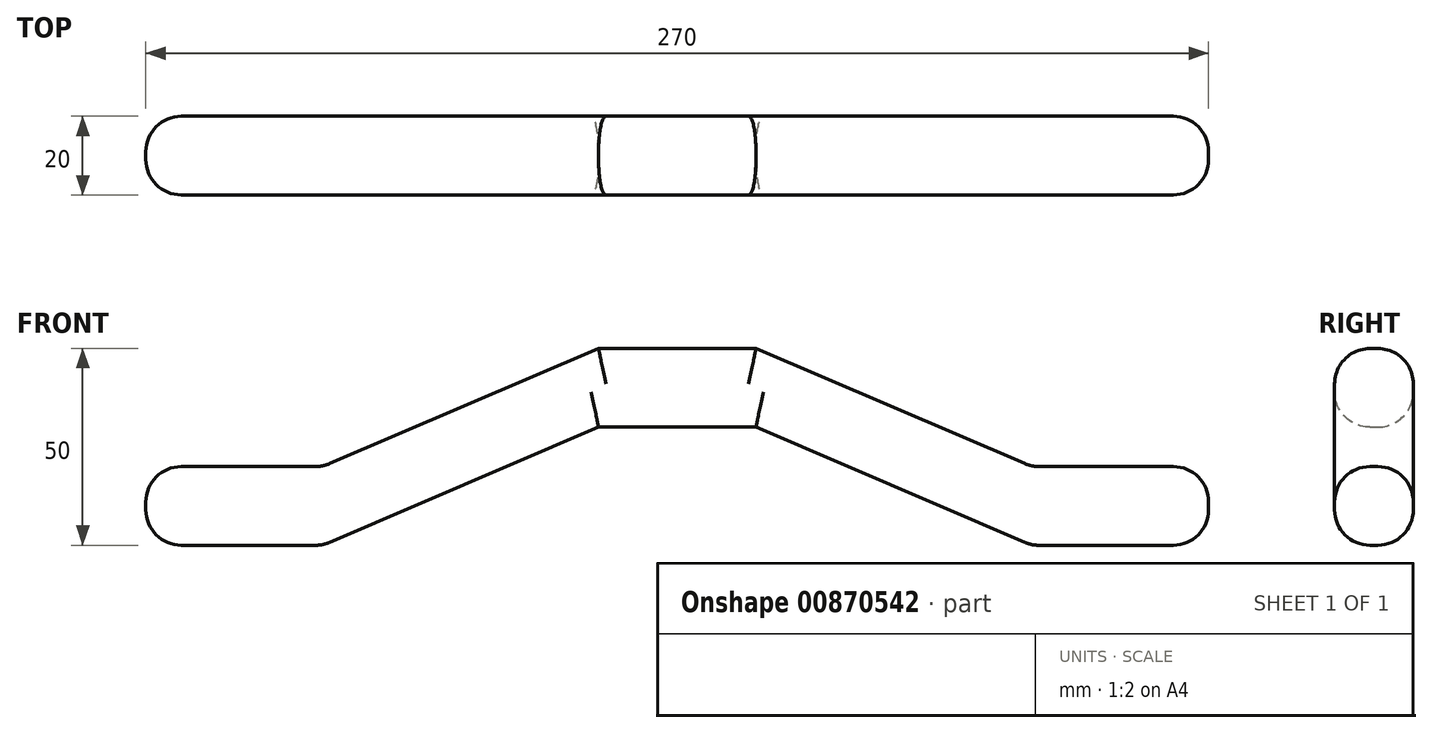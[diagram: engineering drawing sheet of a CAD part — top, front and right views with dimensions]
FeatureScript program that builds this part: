
annotation { "Feature Type Name" : "Feature", "Feature Type Description" : "" }
export const myFeature = defineFeature(function(context is Context, id is Id, definition is map)
    precondition{}
    {
        {
            var Q0;
            Q0=qCreatedBy(makeId("Front.planeOp"),FACE);
            var sketch = newSketch(context, id + "F0", { "sketchPlane" : qUnion([Q0])});
            skLineSegment(sketch, "E0", {"start": v(-65.33, 42.55) * mm, "end": v(-25.33, 42.55) * mm});
            skLineSegment(sketch, "E1", {"start": v(-65.33, 42.55) * mm, "end": v(-135.33, 12.55) * mm});
            skLineSegment(sketch, "E2", {"start": v(-25.33, 42.55) * mm, "end": v(44.67, 12.55) * mm});
            skPoint(sketch, "E3.top.start.orphan", {"position": v(-45.33, 12.55) * mm});
            skPoint(sketch, "E3.bottom.end.orphan", {"position": v(-110.1, 25.55) * mm});
            skPoint(sketch, "E4.right.start.orphan", {"position": v(1.1, 25.55) * mm});
            skLineSegment(sketch, "E5", {"start": v(-135.33, 12.55) * mm, "end": v(-180.33, 12.55) * mm});
            skLineSegment(sketch, "E6", {"start": v(44.67, 12.55) * mm, "end": v(89.67, 12.55) * mm});
            skLineSegment(sketch, "E7.0", {"start": v(-135.33, 32.55) * mm, "end": v(-180.33, 32.55) * mm});
            skLineSegment(sketch, "E8.0", {"start": v(-65.33, 62.55) * mm, "end": v(-25.33, 62.55) * mm});
            skLineSegment(sketch, "E9.0", {"start": v(44.67, 32.55) * mm, "end": v(89.67, 32.55) * mm});
            skLineSegment(sketch, "E10", {"start": v(44.67, 32.55) * mm, "end": v(-25.33, 62.55) * mm});
            skLineSegment(sketch, "E11", {"start": v(-65.33, 62.55) * mm, "end": v(-135.33, 32.55) * mm});
            skLineSegment(sketch, "E12", {"start": v(-180.33, 32.55) * mm, "end": v(-180.33, 12.55) * mm});
            skLineSegment(sketch, "E13", {"start": v(89.67, 12.55) * mm, "end": v(89.67, 32.55) * mm});
            skSolve(sketch);
        }
        {
            var Q0;
            Q0=makeQuery(id+"F0.imprint","IMPRINT",FACE,{"disambiguationData":[TD([[makeQuery(id+"F0.imprint","IMPRINT",EDGE,{"derivedFrom":sQuery(id+"F0.wireOp",EDGE,"E0")}),1.0]])]});
            extrude(context, id + "F1", {"entities" : qUnion([Q0]), "depth" : 20 * mm, "offsetDistance" : 25 * mm});
        }
        {
            var Q0;
            Q0=makeQuery(id+"F1.opExtrude","CAP_FACE",FACE,{"disambiguationData":[OSD([sQuery(id+"F0.wireOp",EDGE,"E0"),sQuery(id+"F0.wireOp",EDGE,"E1"),sQuery(id+"F0.wireOp",EDGE,"E2"),sQuery(id+"F0.wireOp",EDGE,"E5"),sQuery(id+"F0.wireOp",EDGE,"E6"),sQuery(id+"F0.wireOp",EDGE,"E7.0"),sQuery(id+"F0.wireOp",EDGE,"E8.0"),sQuery(id+"F0.wireOp",EDGE,"E9.0"),sQuery(id+"F0.wireOp",EDGE,"E10"),sQuery(id+"F0.wireOp",EDGE,"E11"),sQuery(id+"F0.wireOp",EDGE,"E12"),sQuery(id+"F0.wireOp",EDGE,"E13")])],"isStart":true});
            var Q1;
            Q1=makeQuery(id+"F1.opExtrude","CAP_FACE",FACE,{"disambiguationData":[OSD([sQuery(id+"F0.wireOp",EDGE,"E0"),sQuery(id+"F0.wireOp",EDGE,"E1"),sQuery(id+"F0.wireOp",EDGE,"E2"),sQuery(id+"F0.wireOp",EDGE,"E5"),sQuery(id+"F0.wireOp",EDGE,"E6"),sQuery(id+"F0.wireOp",EDGE,"E7.0"),sQuery(id+"F0.wireOp",EDGE,"E8.0"),sQuery(id+"F0.wireOp",EDGE,"E9.0"),sQuery(id+"F0.wireOp",EDGE,"E10"),sQuery(id+"F0.wireOp",EDGE,"E11"),sQuery(id+"F0.wireOp",EDGE,"E12"),sQuery(id+"F0.wireOp",EDGE,"E13")])],"isStart":false});
            var Q2;
            Q2=makeQuery(id+"F1.opExtrude","SWEPT_FACE",FACE,{"disambiguationData":[OSD([sQuery(id+"F0.wireOp",EDGE,"E7.0")])]});
            var Q3;
            Q3=makeQuery(id+"F1.opExtrude","SWEPT_FACE",FACE,{"disambiguationData":[OSD([sQuery(id+"F0.wireOp",EDGE,"E9.0")])]});
            var Q4;
            Q4=makeQuery(id+"F1.opExtrude","SWEPT_FACE",FACE,{"disambiguationData":[OSD([sQuery(id+"F0.wireOp",EDGE,"E6")])]});
            var Q5;
            Q5=makeQuery(id+"F1.opExtrude","SWEPT_FACE",FACE,{"disambiguationData":[OSD([sQuery(id+"F0.wireOp",EDGE,"E5")])]});
            fillet(context, id + "F2", {"entities" : qUnion([Q0, Q1, Q2, Q3, Q4, Q5]), "radius" : 9 * mm, "tangentPropagation" : true, "allowEdgeOverflow" : false});
        }
    });
